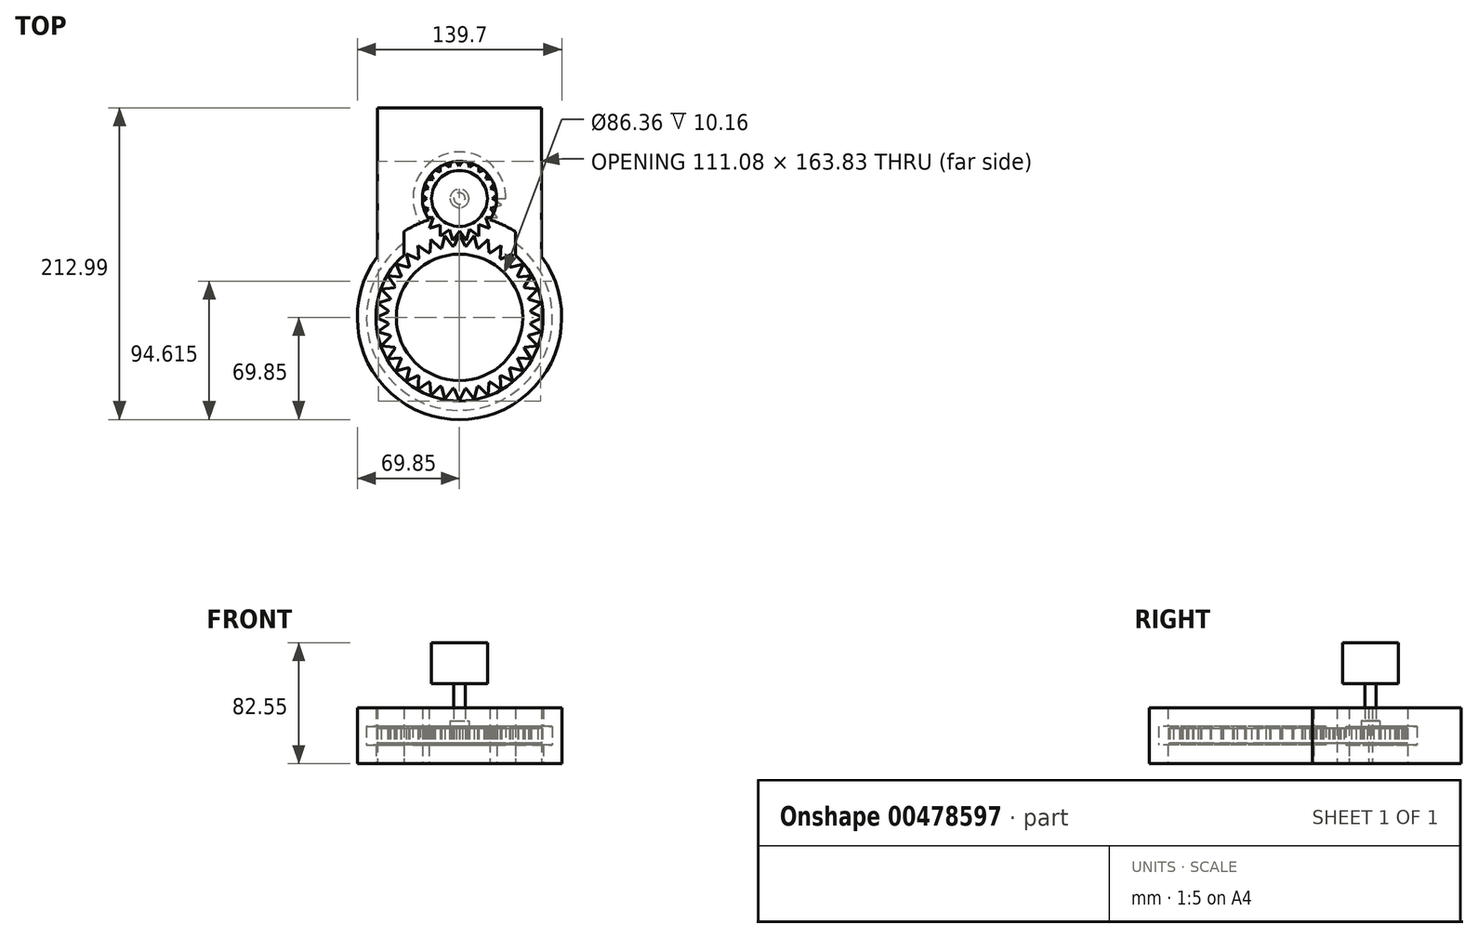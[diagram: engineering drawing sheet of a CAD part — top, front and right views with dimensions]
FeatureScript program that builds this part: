
annotation { "Feature Type Name" : "Feature", "Feature Type Description" : "" }
export const myFeature = defineFeature(function(context is Context, id is Id, definition is map)
    precondition{}
    {
        {
            var Q0;
            Q0=qCreatedBy(makeId("Front.planeOp"),FACE);
            var sketch = newSketch(context, id + "F0", { "sketchPlane" : qUnion([Q0])});
            skLineSegment(sketch, "E0.bottom", {"start": v(57.15, 6.35) * mm, "end": v(63.5, 6.35) * mm});
            skLineSegment(sketch, "E0.top", {"start": v(57.15, -6.35) * mm, "end": v(63.5, -6.35) * mm});
            skLineSegment(sketch, "E0.right", {"start": v(63.5, 6.35) * mm, "end": v(63.5, -6.35) * mm});
            skLineSegment(sketch, "E1", {"start": v(0, 47.25) * mm, "end": v(0, -73.32) * mm, "construction": true});
            skLineSegment(sketch, "E2", {"start": v(57.15, 6.35) * mm, "end": v(57.15, -6.35) * mm});
            skSolve(sketch);
        }
        {
            var Q0;
            Q0=qCreatedBy(makeId("Top.planeOp"),FACE);
            var sketch = newSketch(context, id + "F1", { "sketchPlane" : qUnion([Q0])});
            skArc(sketch, "E3", {"start": v(-38.1, 58.54) * mm, "mid": v(0, -69.85) * mm, "end": v(38.1, 58.54) * mm});
            skArc(sketch, "E4", {"start": v(-38.1, 42.6) * mm, "mid": v(0, -57.15) * mm, "end": v(38.1, 42.6) * mm});
            skLineSegment(sketch, "E5.left", {"start": v(-38.1, 42.6) * mm, "end": v(-38.1, 58.54) * mm});
            skLineSegment(sketch, "E5.right", {"start": v(38.1, 42.6) * mm, "end": v(38.1, 58.54) * mm});
            skLineSegment(sketch, "E6.top", {"start": v(-56.15, 143.14) * mm, "end": v(56.17, 143.14) * mm});
            skLineSegment(sketch, "E6.left", {"start": v(-56.15, 41.54) * mm, "end": v(-56.15, 143.14) * mm});
            skLineSegment(sketch, "E6.right", {"start": v(56.17, 41.53) * mm, "end": v(56.17, 143.14) * mm});
            skArc(sketch, "E7", {"start": v(-56.15, 82.55) * mm, "mid": v(-56.17, 81.28) * mm, "end": v(-56.15, 80) * mm});
            skArc(sketch, "E8", {"start": v(-20.79, 66.68) * mm, "mid": v(0, -69.85) * mm, "end": v(20.79, 66.68) * mm});
            skArc(sketch, "E9", {"start": v(20.79, 66.68) * mm, "mid": v(0, 106.68) * mm, "end": v(-20.79, 66.68) * mm});
            skSolve(sketch);
        }
        {
            var Q0;
            Q0 = qSketchRegion(id + "F1", true);
            extrude(context, id + "F2", {"entities" : qUnion([Q0]), "endBound" : BoundingType.SYMMETRIC, "depth" : 38.1 * mm});
        }
        {
            var Q0;
            Q0 = qSketchRegion(id + "F0", true);
            var Q1;
            Q1=sQuery(id+"F0.wireOp",EDGE,"E1");
            revolve(context, id + "F3", {"operationType" : NewBodyOperationType.REMOVE, "entities" : qUnion([Q0]), "axis" : qUnion([Q1]), "revolveType" : RevolveType.FULL, "oppositeDirection" : true});
        }
        {
            var Q0;
            Q0=qCreatedBy(makeId("Top.planeOp"),FACE);
            var sketch = newSketch(context, id + "F4", { "sketchPlane" : qUnion([Q0])});
            skCircle(sketch, "E10", {"center": v(0, 0) * mm, "radius": 48.9 * mm});
            skLineSegment(sketch, "E11", {"start": v(-3.82, 48.75) * mm, "end": v(0, 56.77) * mm});
            skLineSegment(sketch, "E12", {"start": v(0, 56.77) * mm, "end": v(3.82, 48.75) * mm});
            skLineSegment(sketch, "E13.1.0", {"start": v(-9.86, 55.91) * mm, "end": v(-4.7, 48.67) * mm});
            skLineSegment(sketch, "E13.1.1", {"start": v(-12.23, 47.34) * mm, "end": v(-9.86, 55.91) * mm});
            skLineSegment(sketch, "E13.2.0", {"start": v(-19.42, 53.35) * mm, "end": v(-13.08, 47.11) * mm});
            skLineSegment(sketch, "E13.2.1", {"start": v(-20.26, 44.5) * mm, "end": v(-19.42, 53.35) * mm});
            skLineSegment(sketch, "E14.2.3.0", {"start": v(-28.39, 49.17) * mm, "end": v(-21.07, 44.12) * mm});
            skLineSegment(sketch, "E14.3.3.0", {"start": v(-27.68, 40.3) * mm, "end": v(-28.39, 49.17) * mm});
            skLineSegment(sketch, "E14.2.4.0", {"start": v(-36.5, 43.5) * mm, "end": v(-28.4, 39.8) * mm});
            skLineSegment(sketch, "E14.3.4.0", {"start": v(-34.26, 34.89) * mm, "end": v(-36.5, 43.5) * mm});
            skLineSegment(sketch, "E14.2.5.0", {"start": v(-43.5, 36.5) * mm, "end": v(-34.89, 34.26) * mm});
            skLineSegment(sketch, "E14.3.5.0", {"start": v(-39.8, 28.4) * mm, "end": v(-43.5, 36.5) * mm});
            skLineSegment(sketch, "E14.2.6.0", {"start": v(-49.17, 28.39) * mm, "end": v(-40.3, 27.68) * mm});
            skLineSegment(sketch, "E14.3.6.0", {"start": v(-44.12, 21.07) * mm, "end": v(-49.17, 28.39) * mm});
            skLineSegment(sketch, "E14.2.7.0", {"start": v(-53.35, 19.42) * mm, "end": v(-44.5, 20.26) * mm});
            skLineSegment(sketch, "E14.3.7.0", {"start": v(-47.11, 13.08) * mm, "end": v(-53.35, 19.42) * mm});
            skLineSegment(sketch, "E14.2.8.0", {"start": v(-55.91, 9.86) * mm, "end": v(-47.34, 12.23) * mm});
            skLineSegment(sketch, "E14.3.8.0", {"start": v(-48.67, 4.7) * mm, "end": v(-55.91, 9.86) * mm});
            skLineSegment(sketch, "E14.2.9.0", {"start": v(-56.77, 0) * mm, "end": v(-48.75, 3.82) * mm});
            skLineSegment(sketch, "E14.3.9.0", {"start": v(-48.75, -3.82) * mm, "end": v(-56.77, 0) * mm});
            skLineSegment(sketch, "E15.2.10.0", {"start": v(-55.91, -9.86) * mm, "end": v(-48.67, -4.7) * mm});
            skLineSegment(sketch, "E15.3.10.0", {"start": v(-47.34, -12.23) * mm, "end": v(-55.91, -9.86) * mm});
            skLineSegment(sketch, "E15.2.11.0", {"start": v(-53.35, -19.42) * mm, "end": v(-47.11, -13.08) * mm});
            skLineSegment(sketch, "E15.3.11.0", {"start": v(-44.5, -20.26) * mm, "end": v(-53.35, -19.42) * mm});
            skLineSegment(sketch, "E15.2.12.0", {"start": v(-49.17, -28.39) * mm, "end": v(-44.12, -21.07) * mm});
            skLineSegment(sketch, "E15.3.12.0", {"start": v(-40.3, -27.68) * mm, "end": v(-49.17, -28.39) * mm});
            skLineSegment(sketch, "E15.2.13.0", {"start": v(-43.5, -36.5) * mm, "end": v(-39.8, -28.4) * mm});
            skLineSegment(sketch, "E15.3.13.0", {"start": v(-34.89, -34.26) * mm, "end": v(-43.5, -36.5) * mm});
            skLineSegment(sketch, "E15.2.14.0", {"start": v(-36.5, -43.5) * mm, "end": v(-34.26, -34.89) * mm});
            skLineSegment(sketch, "E15.3.14.0", {"start": v(-28.4, -39.8) * mm, "end": v(-36.5, -43.5) * mm});
            skLineSegment(sketch, "E15.2.15.0", {"start": v(-28.39, -49.17) * mm, "end": v(-27.68, -40.3) * mm});
            skLineSegment(sketch, "E15.3.15.0", {"start": v(-21.07, -44.12) * mm, "end": v(-28.39, -49.17) * mm});
            skLineSegment(sketch, "E15.2.16.0", {"start": v(-19.42, -53.35) * mm, "end": v(-20.26, -44.5) * mm});
            skLineSegment(sketch, "E15.3.16.0", {"start": v(-13.08, -47.11) * mm, "end": v(-19.42, -53.35) * mm});
            skLineSegment(sketch, "E15.2.17.0", {"start": v(-9.86, -55.91) * mm, "end": v(-12.23, -47.34) * mm});
            skLineSegment(sketch, "E15.3.17.0", {"start": v(-4.7, -48.67) * mm, "end": v(-9.86, -55.91) * mm});
            skLineSegment(sketch, "E15.2.18.0", {"start": v(0, -56.77) * mm, "end": v(-3.82, -48.75) * mm});
            skLineSegment(sketch, "E15.3.18.0", {"start": v(3.82, -48.75) * mm, "end": v(0, -56.77) * mm});
            skLineSegment(sketch, "E15.2.19.0", {"start": v(9.86, -55.91) * mm, "end": v(4.7, -48.67) * mm});
            skLineSegment(sketch, "E15.3.19.0", {"start": v(12.23, -47.34) * mm, "end": v(9.86, -55.91) * mm});
            skLineSegment(sketch, "E15.2.20.0", {"start": v(19.42, -53.35) * mm, "end": v(13.08, -47.11) * mm});
            skLineSegment(sketch, "E15.3.20.0", {"start": v(20.26, -44.5) * mm, "end": v(19.42, -53.35) * mm});
            skLineSegment(sketch, "E15.2.21.0", {"start": v(28.39, -49.17) * mm, "end": v(21.07, -44.12) * mm});
            skLineSegment(sketch, "E15.3.21.0", {"start": v(27.68, -40.3) * mm, "end": v(28.39, -49.17) * mm});
            skLineSegment(sketch, "E15.2.22.0", {"start": v(36.5, -43.5) * mm, "end": v(28.4, -39.8) * mm});
            skLineSegment(sketch, "E15.3.22.0", {"start": v(34.26, -34.89) * mm, "end": v(36.5, -43.5) * mm});
            skLineSegment(sketch, "E15.2.23.0", {"start": v(43.5, -36.5) * mm, "end": v(34.89, -34.26) * mm});
            skLineSegment(sketch, "E15.3.23.0", {"start": v(39.8, -28.4) * mm, "end": v(43.5, -36.5) * mm});
            skLineSegment(sketch, "E15.2.24.0", {"start": v(49.17, -28.39) * mm, "end": v(40.3, -27.68) * mm});
            skLineSegment(sketch, "E15.3.24.0", {"start": v(44.12, -21.07) * mm, "end": v(49.17, -28.39) * mm});
            skLineSegment(sketch, "E15.2.25.0", {"start": v(53.35, -19.42) * mm, "end": v(44.5, -20.26) * mm});
            skLineSegment(sketch, "E15.3.25.0", {"start": v(47.11, -13.08) * mm, "end": v(53.35, -19.42) * mm});
            skLineSegment(sketch, "E15.2.26.0", {"start": v(55.91, -9.86) * mm, "end": v(47.34, -12.23) * mm});
            skLineSegment(sketch, "E15.3.26.0", {"start": v(48.67, -4.7) * mm, "end": v(55.91, -9.86) * mm});
            skLineSegment(sketch, "E15.2.27.0", {"start": v(56.77, 0) * mm, "end": v(48.75, -3.82) * mm});
            skLineSegment(sketch, "E15.3.27.0", {"start": v(48.75, 3.82) * mm, "end": v(56.77, 0) * mm});
            skLineSegment(sketch, "E15.2.28.0", {"start": v(55.91, 9.86) * mm, "end": v(48.67, 4.7) * mm});
            skLineSegment(sketch, "E15.3.28.0", {"start": v(47.34, 12.23) * mm, "end": v(55.91, 9.86) * mm});
            skLineSegment(sketch, "E15.2.29.0", {"start": v(53.35, 19.42) * mm, "end": v(47.11, 13.08) * mm});
            skLineSegment(sketch, "E15.3.29.0", {"start": v(44.5, 20.26) * mm, "end": v(53.35, 19.42) * mm});
            skLineSegment(sketch, "E16.2.30.0", {"start": v(49.17, 28.39) * mm, "end": v(44.12, 21.07) * mm});
            skLineSegment(sketch, "E16.3.30.0", {"start": v(40.3, 27.68) * mm, "end": v(49.17, 28.39) * mm});
            skLineSegment(sketch, "E16.2.31.0", {"start": v(43.5, 36.5) * mm, "end": v(39.8, 28.4) * mm});
            skLineSegment(sketch, "E16.3.31.0", {"start": v(34.89, 34.26) * mm, "end": v(43.5, 36.5) * mm});
            skLineSegment(sketch, "E16.2.32.0", {"start": v(36.5, 43.5) * mm, "end": v(34.26, 34.89) * mm});
            skLineSegment(sketch, "E16.3.32.0", {"start": v(28.4, 39.8) * mm, "end": v(36.5, 43.5) * mm});
            skLineSegment(sketch, "E16.2.33.0", {"start": v(28.39, 49.17) * mm, "end": v(27.68, 40.3) * mm});
            skLineSegment(sketch, "E16.3.33.0", {"start": v(21.07, 44.12) * mm, "end": v(28.39, 49.17) * mm});
            skLineSegment(sketch, "E16.2.34.0", {"start": v(19.42, 53.35) * mm, "end": v(20.26, 44.5) * mm});
            skLineSegment(sketch, "E16.3.34.0", {"start": v(13.08, 47.11) * mm, "end": v(19.42, 53.35) * mm});
            skLineSegment(sketch, "E16.2.35.0", {"start": v(9.86, 55.91) * mm, "end": v(12.23, 47.34) * mm});
            skLineSegment(sketch, "E16.3.35.0", {"start": v(4.7, 48.67) * mm, "end": v(9.86, 55.91) * mm});
            skCircle(sketch, "E17", {"center": v(0, 0) * mm, "radius": 43.18 * mm});
            skSolve(sketch);
        }
        {
            var Q0;
            Q0 = qSketchRegion(id + "F4", true);
            extrude(context, id + "F5", {"entities" : qUnion([Q0]), "endBound" : BoundingType.SYMMETRIC, "depth" : 10.16 * mm});
        }
        {
            var Q0;
            Q0=qCreatedBy(makeId("Top.planeOp"),FACE);
            var sketch = newSketch(context, id + "F6", { "sketchPlane" : qUnion([Q0])});
            skCircle(sketch, "E18", {"center": v(0, 81.28) * mm, "radius": 22.23 * mm});
            skLineSegment(sketch, "E19", {"start": v(0, 59.06) * mm, "end": v(4.58, 52.65) * mm});
            skLineSegment(sketch, "E20", {"start": v(4.58, 52.65) * mm, "end": v(6.93, 60.16) * mm});
            skLineSegment(sketch, "E21.1.0", {"start": v(13.2, 55.46) * mm, "end": v(13.12, 63.34) * mm});
            skLineSegment(sketch, "E21.1.1", {"start": v(6.87, 60.14) * mm, "end": v(13.2, 55.46) * mm});
            skLineSegment(sketch, "E21.2.0", {"start": v(20.53, 60.8) * mm, "end": v(18.02, 68.27) * mm});
            skLineSegment(sketch, "E21.2.1", {"start": v(13.06, 63.3) * mm, "end": v(20.53, 60.8) * mm});
            skLineSegment(sketch, "E22.1.3.0", {"start": v(25.85, 68.15) * mm, "end": v(21.16, 74.47) * mm});
            skLineSegment(sketch, "E22.3.3.0", {"start": v(17.98, 68.22) * mm, "end": v(25.85, 68.15) * mm});
            skLineSegment(sketch, "E22.1.4.0", {"start": v(28.65, 76.79) * mm, "end": v(22.22, 81.34) * mm});
            skLineSegment(sketch, "E22.3.4.0", {"start": v(21.14, 74.41) * mm, "end": v(28.65, 76.79) * mm});
            skLineSegment(sketch, "E22.1.5.0", {"start": v(28.63, 85.86) * mm, "end": v(21.12, 88.2) * mm});
            skLineSegment(sketch, "E22.3.5.0", {"start": v(22.22, 81.28) * mm, "end": v(28.63, 85.86) * mm});
            skLineSegment(sketch, "E22.1.6.0", {"start": v(25.82, 94.48) * mm, "end": v(17.94, 94.4) * mm});
            skLineSegment(sketch, "E22.3.6.0", {"start": v(21.14, 88.15) * mm, "end": v(25.82, 94.48) * mm});
            skLineSegment(sketch, "E22.1.7.0", {"start": v(20.47, 101.81) * mm, "end": v(13.01, 99.3) * mm});
            skLineSegment(sketch, "E22.3.7.0", {"start": v(17.98, 94.34) * mm, "end": v(20.47, 101.81) * mm});
            skLineSegment(sketch, "E22.1.8.0", {"start": v(13.13, 107.13) * mm, "end": v(6.8, 102.44) * mm});
            skLineSegment(sketch, "E22.3.8.0", {"start": v(13.06, 99.26) * mm, "end": v(13.13, 107.13) * mm});
            skLineSegment(sketch, "E22.1.9.0", {"start": v(4.5, 109.93) * mm, "end": v(-0.06, 103.5) * mm});
            skLineSegment(sketch, "E22.3.9.0", {"start": v(6.87, 102.42) * mm, "end": v(4.5, 109.93) * mm});
            skLineSegment(sketch, "E22.1.10.0", {"start": v(-4.58, 109.91) * mm, "end": v(-6.93, 102.4) * mm});
            skLineSegment(sketch, "E22.3.10.0", {"start": v(0, 103.5) * mm, "end": v(-4.58, 109.91) * mm});
            skLineSegment(sketch, "E22.1.11.0", {"start": v(-13.2, 107.1) * mm, "end": v(-13.12, 99.22) * mm});
            skLineSegment(sketch, "E22.3.11.0", {"start": v(-6.87, 102.42) * mm, "end": v(-13.2, 107.1) * mm});
            skLineSegment(sketch, "E23.1.12.0", {"start": v(-20.53, 101.75) * mm, "end": v(-18.02, 94.3) * mm});
            skLineSegment(sketch, "E23.3.12.0", {"start": v(-13.06, 99.26) * mm, "end": v(-20.53, 101.75) * mm});
            skLineSegment(sketch, "E23.1.13.0", {"start": v(-25.85, 94.4) * mm, "end": v(-21.16, 88.09) * mm});
            skLineSegment(sketch, "E23.3.13.0", {"start": v(-17.98, 94.34) * mm, "end": v(-25.85, 94.4) * mm});
            skLineSegment(sketch, "E23.1.14.0", {"start": v(-28.65, 85.77) * mm, "end": v(-22.22, 81.22) * mm});
            skLineSegment(sketch, "E23.3.14.0", {"start": v(-21.14, 88.15) * mm, "end": v(-28.65, 85.77) * mm});
            skLineSegment(sketch, "E23.1.15.0", {"start": v(-28.63, 76.7) * mm, "end": v(-21.12, 74.35) * mm});
            skLineSegment(sketch, "E23.3.15.0", {"start": v(-22.22, 81.28) * mm, "end": v(-28.63, 76.7) * mm});
            skLineSegment(sketch, "E23.1.16.0", {"start": v(-25.82, 68.08) * mm, "end": v(-17.94, 68.16) * mm});
            skLineSegment(sketch, "E23.3.16.0", {"start": v(-21.14, 74.41) * mm, "end": v(-25.82, 68.08) * mm});
            skLineSegment(sketch, "E23.1.17.0", {"start": v(-20.47, 60.75) * mm, "end": v(-13.01, 63.26) * mm});
            skLineSegment(sketch, "E23.3.17.0", {"start": v(-17.98, 68.22) * mm, "end": v(-20.47, 60.75) * mm});
            skLineSegment(sketch, "E23.1.18.0", {"start": v(-13.13, 55.43) * mm, "end": v(-6.8, 60.12) * mm});
            skLineSegment(sketch, "E23.3.18.0", {"start": v(-13.06, 63.3) * mm, "end": v(-13.13, 55.43) * mm});
            skLineSegment(sketch, "E23.1.19.0", {"start": v(-4.5, 52.63) * mm, "end": v(0.06, 59.06) * mm});
            skLineSegment(sketch, "E23.3.19.0", {"start": v(-6.87, 60.14) * mm, "end": v(-4.5, 52.63) * mm});
            skSolve(sketch);
        }
        {
            var Q0;
            Q0 = qSketchRegion(id + "F6", true);
            var Q1;
            {var subQ0=sQuery(id+"F6.wireOp",EDGE,"E18");var subQ17=makeQuery(id+"F6.imprint","INTERSECT",VERTEX,{"derivedFrom":[subQ0,sQuery(id+"F6.wireOp",EDGE,"E22.1.4.0")]});Q1=makeQuery(id+"F6.imprint","IMPRINT",FACE,{"disambiguationData":[TD([[makeQuery(id+"F6.imprint","IMPRINT",EDGE,{"disambiguationData":[TD([[subQ17,1.0]])],"derivedFrom":subQ0}),1.0]])]});}
            extrude(context, id + "F7", {"entities" : qUnion([Q0, Q1]), "endBound" : BoundingType.SYMMETRIC, "depth" : 10.16 * mm});
        }
        {
            var Q0;
            Q0=qCreatedBy(makeId("Front.planeOp"),FACE);
            cPlane(context, id + "F8", {"entities" : qUnion([Q0]), "cplaneType" : CPlaneType.OFFSET, "offset" : 81.28 * mm, "oppositeDirection" : true, "width" : 152.4 * mm, "height" : 152.4 * mm});
        }
        {
            var Q0;
            Q0=qCreatedBy(id+"F8.planeOp",FACE);
            var sketch = newSketch(context, id + "F9", { "sketchPlane" : qUnion([Q0])});
            skLineSegment(sketch, "E24", {"start": v(0, 0) * mm, "end": v(0, 63.5) * mm});
            skLineSegment(sketch, "E25", {"start": v(0, 0) * mm, "end": v(-6.38, 0) * mm});
            skLineSegment(sketch, "E26", {"start": v(-6.38, 0) * mm, "end": v(-6.38, 10.16) * mm});
            skLineSegment(sketch, "E27", {"start": v(-6.38, 10.16) * mm, "end": v(-3.84, 10.16) * mm});
            skLineSegment(sketch, "E28", {"start": v(-3.84, 10.16) * mm, "end": v(-3.84, 35.56) * mm});
            skLineSegment(sketch, "E29", {"start": v(-3.84, 35.56) * mm, "end": v(-19.08, 35.56) * mm});
            skLineSegment(sketch, "E30", {"start": v(-19.08, 35.56) * mm, "end": v(-19.08, 63.5) * mm});
            skLineSegment(sketch, "E31", {"start": v(0, 63.5) * mm, "end": v(-19.08, 63.5) * mm});
            skSolve(sketch);
        }
        {
            var Q0;
            Q0 = qSketchRegion(id + "F9", true);
            var Q1;
            Q1=sQuery(id+"F9.wireOp",EDGE,"E24");
            revolve(context, id + "F10", {"operationType" : NewBodyOperationType.ADD, "entities" : qUnion([Q0]), "axis" : qUnion([Q1]), "revolveType" : RevolveType.FULL});
        }
        {
            var Q0;
            Q0=qCreatedBy(id+"F8.planeOp",FACE);
            var sketch = newSketch(context, id + "F11", { "sketchPlane" : qUnion([Q0])});
            skLineSegment(sketch, "E32.bottom", {"start": v(25.4, 6.35) * mm, "end": v(31.75, 6.35) * mm});
            skLineSegment(sketch, "E32.top", {"start": v(25.4, -6.35) * mm, "end": v(31.75, -6.35) * mm});
            skLineSegment(sketch, "E32.left", {"start": v(25.4, 6.35) * mm, "end": v(25.4, -6.35) * mm});
            skLineSegment(sketch, "E32.right", {"start": v(31.75, 6.35) * mm, "end": v(31.75, -6.35) * mm});
            skSolve(sketch);
        }
        {
            var Q0;
            Q0 = qSketchRegion(id + "F11", true);
            var Q1;
            Q1=makeQuery(id+"F10.opRevolve","SWEPT_FACE",FACE,{"disambiguationData":[OSD([sQuery(id+"F9.wireOp",EDGE,"E28")])]});
            revolve(context, id + "F12", {"operationType" : NewBodyOperationType.REMOVE, "entities" : qUnion([Q0]), "axis" : qUnion([Q1]), "revolveType" : RevolveType.ONE_DIRECTION, "oppositeDirection" : true, "angle" : 220 * degree});
        }
    });
